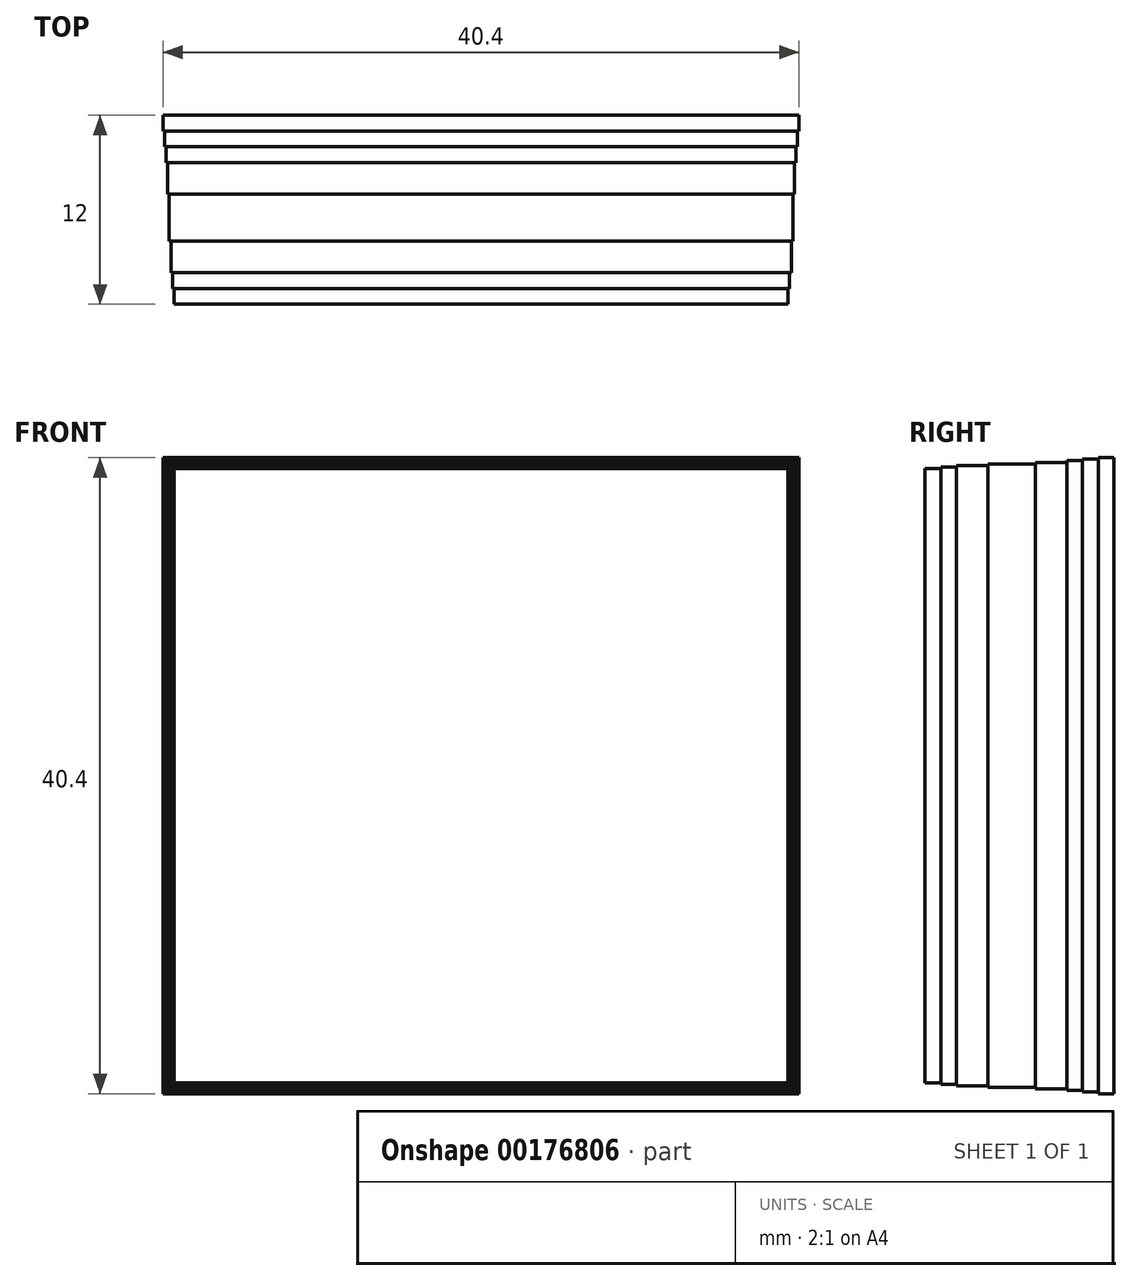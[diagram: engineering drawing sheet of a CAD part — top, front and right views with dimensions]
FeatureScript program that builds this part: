
annotation { "Feature Type Name" : "Feature", "Feature Type Description" : "" }
export const myFeature = defineFeature(function(context is Context, id is Id, definition is map)
    precondition{}
    {
        {
            var Q0;
            Q0=qCreatedBy(makeId("Front.planeOp"),FACE);
            var sketch = newSketch(context, id + "F0", { "sketchPlane" : qUnion([Q0])});
            skLineSegment(sketch, "E0.bottom", {"start": v(20, -20) * mm, "end": v(-20, -20) * mm});
            skLineSegment(sketch, "E0.top", {"start": v(20, 20) * mm, "end": v(-20, 20) * mm});
            skLineSegment(sketch, "E0.left", {"start": v(20, -20) * mm, "end": v(20, 20) * mm});
            skLineSegment(sketch, "E0.right", {"start": v(-20, -20) * mm, "end": v(-20, 20) * mm});
            skPoint(sketch, "E0.middle", {"position": v(0, 0) * mm});
            skSolve(sketch);
        }
        {
            var Q0;
            Q0 = qSketchRegion(id + "F0", true);
            extrude(context, id + "F1", {"entities" : qUnion([Q0]), "depth" : 1 * mm});
        }
        {
            var Q0;
            Q0=makeQuery(id+"F1.opExtrude","CAP_FACE",FACE,{"disambiguationData":[OSD([sQuery(id+"F0.wireOp",EDGE,"E0.bottom"),sQuery(id+"F0.wireOp",EDGE,"E0.top"),sQuery(id+"F0.wireOp",EDGE,"E0.left"),sQuery(id+"F0.wireOp",EDGE,"E0.right")])],"isStart":false});
            var sketch = newSketch(context, id + "F2", { "sketchPlane" : qUnion([Q0])});
            skLineSegment(sketch, "E1.bottom", {"start": v(19.9, -19.9) * mm, "end": v(-19.9, -19.9) * mm});
            skLineSegment(sketch, "E1.top", {"start": v(19.9, 19.9) * mm, "end": v(-19.9, 19.9) * mm});
            skLineSegment(sketch, "E1.left", {"start": v(19.9, -19.9) * mm, "end": v(19.9, 19.9) * mm});
            skLineSegment(sketch, "E1.right", {"start": v(-19.9, -19.9) * mm, "end": v(-19.9, 19.9) * mm});
            skPoint(sketch, "E1.middle", {"position": v(0, 0) * mm});
            skSolve(sketch);
        }
        {
            var Q0;
            Q0 = qSketchRegion(id + "F2", true);
            extrude(context, id + "F3", {"entities" : qUnion([Q0]), "operationType" : NewBodyOperationType.ADD, "depth" : 2 * mm});
        }
        {
            var Q0;
            Q0=makeQuery(id+"F3.opExtrude","CAP_FACE",FACE,{"disambiguationData":[OSD([sQuery(id+"F2.wireOp",EDGE,"E1.bottom"),sQuery(id+"F2.wireOp",EDGE,"E1.top"),sQuery(id+"F2.wireOp",EDGE,"E1.left"),sQuery(id+"F2.wireOp",EDGE,"E1.right")])],"isStart":false});
            var sketch = newSketch(context, id + "F4", { "sketchPlane" : qUnion([Q0])});
            skLineSegment(sketch, "E2.bottom", {"start": v(19.8, -19.8) * mm, "end": v(-19.8, -19.8) * mm});
            skLineSegment(sketch, "E2.top", {"start": v(19.8, 19.8) * mm, "end": v(-19.8, 19.8) * mm});
            skLineSegment(sketch, "E2.left", {"start": v(19.8, -19.8) * mm, "end": v(19.8, 19.8) * mm});
            skLineSegment(sketch, "E2.right", {"start": v(-19.8, -19.8) * mm, "end": v(-19.8, 19.8) * mm});
            skPoint(sketch, "E2.middle", {"position": v(0, 0) * mm});
            skSolve(sketch);
        }
        {
            var Q0;
            Q0 = qSketchRegion(id + "F4", true);
            extrude(context, id + "F5", {"entities" : qUnion([Q0]), "operationType" : NewBodyOperationType.ADD, "depth" : 3 * mm});
        }
        {
            var Q0;
            Q0=makeQuery(id+"F5.opExtrude","CAP_FACE",FACE,{"disambiguationData":[OSD([sQuery(id+"F4.wireOp",EDGE,"E2.bottom"),sQuery(id+"F4.wireOp",EDGE,"E2.top"),sQuery(id+"F4.wireOp",EDGE,"E2.left"),sQuery(id+"F4.wireOp",EDGE,"E2.right")])],"isStart":false});
            var sketch = newSketch(context, id + "F6", { "sketchPlane" : qUnion([Q0])});
            skLineSegment(sketch, "E3.bottom", {"start": v(19.7, -19.7) * mm, "end": v(-19.7, -19.7) * mm});
            skLineSegment(sketch, "E3.top", {"start": v(19.7, 19.7) * mm, "end": v(-19.7, 19.7) * mm});
            skLineSegment(sketch, "E3.left", {"start": v(19.7, -19.7) * mm, "end": v(19.7, 19.7) * mm});
            skLineSegment(sketch, "E3.right", {"start": v(-19.7, -19.7) * mm, "end": v(-19.7, 19.7) * mm});
            skPoint(sketch, "E3.middle", {"position": v(0, 0) * mm});
            skSolve(sketch);
        }
        {
            var Q0;
            Q0 = qSketchRegion(id + "F6", true);
            extrude(context, id + "F7", {"entities" : qUnion([Q0]), "operationType" : NewBodyOperationType.ADD, "depth" : 1 * mm});
        }
        {
            var Q0;
            Q0=makeQuery(id+"F7.opExtrude","CAP_FACE",FACE,{"disambiguationData":[OSD([sQuery(id+"F6.wireOp",EDGE,"E3.bottom"),sQuery(id+"F6.wireOp",EDGE,"E3.top"),sQuery(id+"F6.wireOp",EDGE,"E3.left"),sQuery(id+"F6.wireOp",EDGE,"E3.right")])],"isStart":false});
            var sketch = newSketch(context, id + "F8", { "sketchPlane" : qUnion([Q0])});
            skLineSegment(sketch, "E4.bottom", {"start": v(19.7, -19.7) * mm, "end": v(-19.7, -19.7) * mm});
            skLineSegment(sketch, "E4.top", {"start": v(19.7, 19.7) * mm, "end": v(-19.7, 19.7) * mm});
            skLineSegment(sketch, "E4.left", {"start": v(19.7, -19.7) * mm, "end": v(19.7, 19.7) * mm});
            skLineSegment(sketch, "E4.right", {"start": v(-19.7, -19.7) * mm, "end": v(-19.7, 19.7) * mm});
            skPoint(sketch, "E4.middle", {"position": v(0, 0) * mm});
            skSolve(sketch);
        }
        {
            var Q0;
            Q0 = qSketchRegion(id + "F8", true);
            extrude(context, id + "F9", {"entities" : qUnion([Q0]), "operationType" : NewBodyOperationType.ADD, "depth" : 1 * mm});
        }
        {
            var Q0;
            Q0=makeQuery(id+"F9.opExtrude","CAP_FACE",FACE,{"disambiguationData":[OSD([sQuery(id+"F8.wireOp",EDGE,"E4.bottom"),sQuery(id+"F8.wireOp",EDGE,"E4.top"),sQuery(id+"F8.wireOp",EDGE,"E4.left"),sQuery(id+"F8.wireOp",EDGE,"E4.right")])],"isStart":false});
            var sketch = newSketch(context, id + "F10", { "sketchPlane" : qUnion([Q0])});
            skLineSegment(sketch, "E5.bottom", {"start": v(19.6, -19.6) * mm, "end": v(-19.6, -19.6) * mm});
            skLineSegment(sketch, "E5.top", {"start": v(19.6, 19.6) * mm, "end": v(-19.6, 19.6) * mm});
            skLineSegment(sketch, "E5.left", {"start": v(19.6, -19.6) * mm, "end": v(19.6, 19.6) * mm});
            skLineSegment(sketch, "E5.right", {"start": v(-19.6, -19.6) * mm, "end": v(-19.6, 19.6) * mm});
            skPoint(sketch, "E5.middle", {"position": v(0, 0) * mm});
            skSolve(sketch);
        }
        {
            var Q0;
            Q0 = qSketchRegion(id + "F10", true);
            extrude(context, id + "F11", {"entities" : qUnion([Q0]), "operationType" : NewBodyOperationType.ADD, "depth" : 1 * mm});
        }
        {
            var Q0;
            Q0=makeQuery(id+"F11.opExtrude","CAP_FACE",FACE,{"disambiguationData":[OSD([sQuery(id+"F10.wireOp",EDGE,"E5.bottom"),sQuery(id+"F10.wireOp",EDGE,"E5.top"),sQuery(id+"F10.wireOp",EDGE,"E5.left"),sQuery(id+"F10.wireOp",EDGE,"E5.right")])],"isStart":false});
            var sketch = newSketch(context, id + "F12", { "sketchPlane" : qUnion([Q0])});
            skLineSegment(sketch, "E6.bottom", {"start": v(19.5, -19.5) * mm, "end": v(-19.5, -19.5) * mm});
            skLineSegment(sketch, "E6.top", {"start": v(19.5, 19.5) * mm, "end": v(-19.5, 19.5) * mm});
            skLineSegment(sketch, "E6.left", {"start": v(19.5, -19.5) * mm, "end": v(19.5, 19.5) * mm});
            skLineSegment(sketch, "E6.right", {"start": v(-19.5, -19.5) * mm, "end": v(-19.5, 19.5) * mm});
            skPoint(sketch, "E6.middle", {"position": v(0, 0) * mm});
            skSolve(sketch);
        }
        {
            var Q0;
            Q0 = qSketchRegion(id + "F12", true);
            extrude(context, id + "F13", {"entities" : qUnion([Q0]), "operationType" : NewBodyOperationType.ADD, "depth" : 1 * mm});
        }
        {
            var Q0;
            Q0=makeQuery(id+"F1.opExtrude","CAP_FACE",FACE,{"disambiguationData":[OSD([sQuery(id+"F0.wireOp",EDGE,"E0.bottom"),sQuery(id+"F0.wireOp",EDGE,"E0.top"),sQuery(id+"F0.wireOp",EDGE,"E0.left"),sQuery(id+"F0.wireOp",EDGE,"E0.right")])],"isStart":true});
            var sketch = newSketch(context, id + "F14", { "sketchPlane" : qUnion([Q0])});
            skLineSegment(sketch, "E7.bottom", {"start": v(-20.1, 20.1) * mm, "end": v(20.1, 20.1) * mm});
            skLineSegment(sketch, "E7.top", {"start": v(-20.1, -20.1) * mm, "end": v(20.1, -20.1) * mm});
            skLineSegment(sketch, "E7.left", {"start": v(-20.1, 20.1) * mm, "end": v(-20.1, -20.1) * mm});
            skLineSegment(sketch, "E7.right", {"start": v(20.1, 20.1) * mm, "end": v(20.1, -20.1) * mm});
            skPoint(sketch, "E7.middle", {"position": v(0, 0) * mm});
            skSolve(sketch);
        }
        {
            var Q0;
            Q0 = qSketchRegion(id + "F14", true);
            extrude(context, id + "F15", {"entities" : qUnion([Q0]), "operationType" : NewBodyOperationType.ADD, "depth" : 1 * mm});
        }
        {
            var Q0;
            Q0=makeQuery(id+"F15.opExtrude","CAP_FACE",FACE,{"disambiguationData":[OSD([sQuery(id+"F14.wireOp",EDGE,"E7.bottom"),sQuery(id+"F14.wireOp",EDGE,"E7.top"),sQuery(id+"F14.wireOp",EDGE,"E7.left"),sQuery(id+"F14.wireOp",EDGE,"E7.right")])],"isStart":false});
            var sketch = newSketch(context, id + "F16", { "sketchPlane" : qUnion([Q0])});
            skLineSegment(sketch, "E8.bottom", {"start": v(20.2, 20.2) * mm, "end": v(-20.2, 20.2) * mm});
            skLineSegment(sketch, "E8.top", {"start": v(20.2, -20.2) * mm, "end": v(-20.2, -20.2) * mm});
            skLineSegment(sketch, "E8.left", {"start": v(20.2, 20.2) * mm, "end": v(20.2, -20.2) * mm});
            skLineSegment(sketch, "E8.right", {"start": v(-20.2, 20.2) * mm, "end": v(-20.2, -20.2) * mm});
            skPoint(sketch, "E8.middle", {"position": v(0, 0) * mm});
            skSolve(sketch);
        }
        {
            var Q0;
            Q0 = qSketchRegion(id + "F16", true);
            extrude(context, id + "F17", {"entities" : qUnion([Q0]), "operationType" : NewBodyOperationType.ADD, "depth" : 1 * mm});
        }
    });
